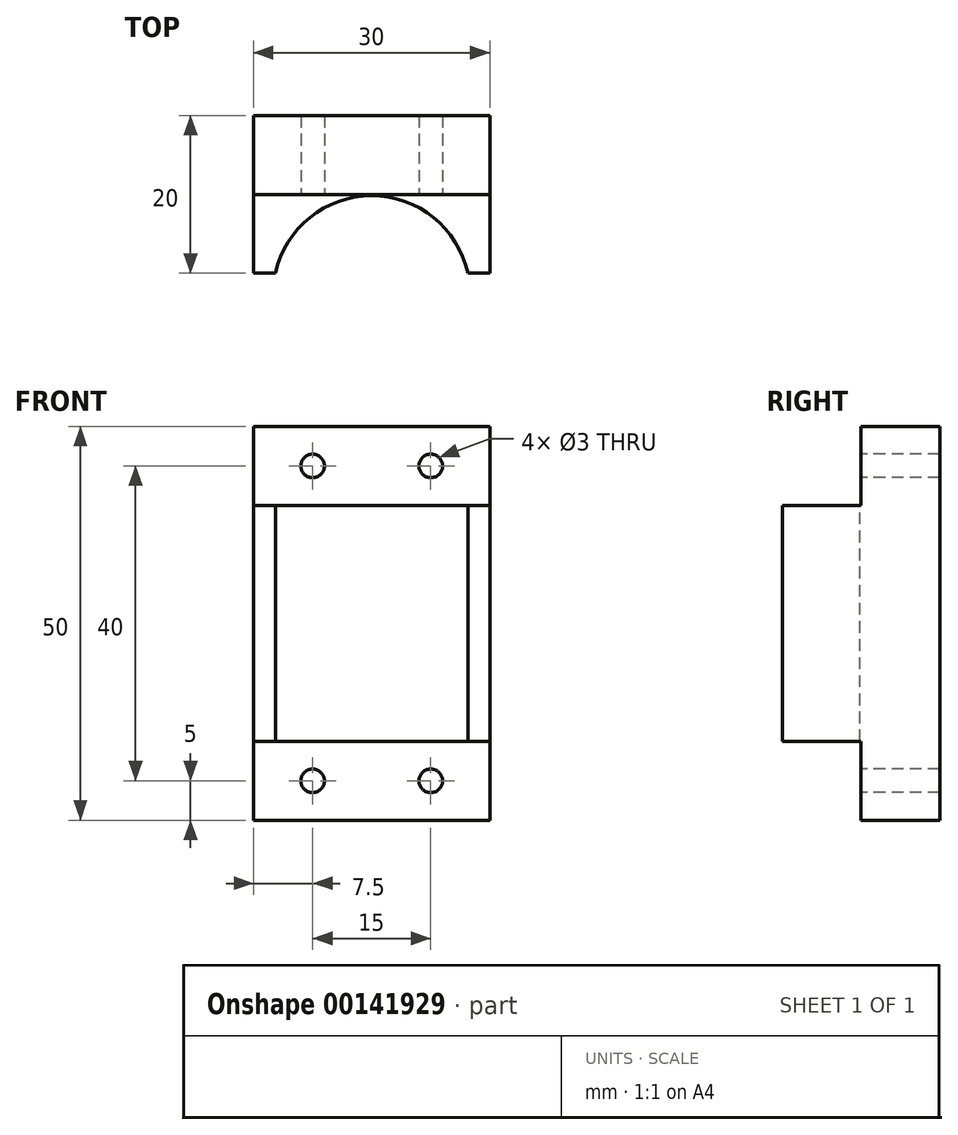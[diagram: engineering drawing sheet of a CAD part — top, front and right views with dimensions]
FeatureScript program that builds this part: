
annotation { "Feature Type Name" : "Feature", "Feature Type Description" : "" }
export const myFeature = defineFeature(function(context is Context, id is Id, definition is map)
    precondition{}
    {
        {
            var Q0;
            Q0=qCreatedBy(makeId("Front.planeOp"),FACE);
            var sketch = newSketch(context, id + "F0", { "sketchPlane" : qUnion([Q0])});
            skLineSegment(sketch, "E0.bottom", {"start": v(15, 25) * mm, "end": v(-15, 25) * mm});
            skLineSegment(sketch, "E0.top", {"start": v(15, -25) * mm, "end": v(-15, -25) * mm});
            skLineSegment(sketch, "E0.left", {"start": v(15, 25) * mm, "end": v(15, -25) * mm});
            skLineSegment(sketch, "E0.right", {"start": v(-15, 25) * mm, "end": v(-15, -25) * mm});
            skPoint(sketch, "E0.middle", {"position": v(0, 0) * mm});
            skSolve(sketch);
        }
        {
            var Q0;
            Q0 = qSketchRegion(id + "F0", true);
            extrude(context, id + "F1", {"entities" : qUnion([Q0]), "depth" : 10 * mm});
        }
        {
            var Q0;
            Q0=makeQuery(id+"F1.opExtrude","CAP_FACE",FACE,{"disambiguationData":[OSD([sQuery(id+"F0.wireOp",EDGE,"E0.bottom"),sQuery(id+"F0.wireOp",EDGE,"E0.top"),sQuery(id+"F0.wireOp",EDGE,"E0.left"),sQuery(id+"F0.wireOp",EDGE,"E0.right")])],"isStart":false});
            var sketch = newSketch(context, id + "F2", { "sketchPlane" : qUnion([Q0])});
            skCircle(sketch, "E1", {"center": v(7.5, -20) * mm, "radius": 1.5 * mm});
            skCircle(sketch, "E2", {"center": v(-7.5, -20) * mm, "radius": 1.5 * mm});
            skCircle(sketch, "E3", {"center": v(7.5, 20) * mm, "radius": 1.5 * mm});
            skCircle(sketch, "E4", {"center": v(-7.5, 20) * mm, "radius": 1.5 * mm});
            skSolve(sketch);
        }
        {
            var Q0;
            Q0 = qSketchRegion(id + "F2", true);
            extrude(context, id + "F3", {"entities" : qUnion([Q0]), "operationType" : NewBodyOperationType.REMOVE, "endBound" : BoundingType.THROUGH_ALL, "oppositeDirection" : true, "depth" : 25 * mm});
        }
        {
            var Q0;
            Q0=makeQuery(id+"F1.opExtrude","CAP_FACE",FACE,{"disambiguationData":[OSD([sQuery(id+"F0.wireOp",EDGE,"E0.bottom"),sQuery(id+"F0.wireOp",EDGE,"E0.top"),sQuery(id+"F0.wireOp",EDGE,"E0.left"),sQuery(id+"F0.wireOp",EDGE,"E0.right")])],"isStart":false});
            var sketch = newSketch(context, id + "F4", { "sketchPlane" : qUnion([Q0])});
            skLineSegment(sketch, "E5.bottom", {"start": v(15, 15) * mm, "end": v(-15, 15) * mm});
            skLineSegment(sketch, "E5.top", {"start": v(15, -15) * mm, "end": v(-15, -15) * mm});
            skLineSegment(sketch, "E5.left", {"start": v(15, 15) * mm, "end": v(15, -15) * mm});
            skLineSegment(sketch, "E5.right", {"start": v(-15, 15) * mm, "end": v(-15, -15) * mm});
            skPoint(sketch, "E5.middle", {"position": v(0, 0) * mm});
            skSolve(sketch);
        }
        {
            var Q0;
            Q0 = qSketchRegion(id + "F4", true);
            extrude(context, id + "F5", {"entities" : qUnion([Q0]), "operationType" : NewBodyOperationType.ADD, "depth" : 10 * mm});
        }
        {
            var Q0;
            Q0=qCreatedBy(makeId("Top.planeOp"),FACE);
            var sketch = newSketch(context, id + "F6", { "sketchPlane" : qUnion([Q0])});
            skCircle(sketch, "E6", {"center": v(0, -22.67) * mm, "radius": 12.5 * mm});
            skSolve(sketch);
        }
        {
            var Q0;
            Q0 = qSketchRegion(id + "F6", true);
            extrude(context, id + "F7", {"entities" : qUnion([Q0]), "operationType" : NewBodyOperationType.REMOVE, "endBound" : BoundingType.THROUGH_ALL, "oppositeDirection" : true, "depth" : 25 * mm});
        }
        {
            var Q0;
            Q0 = qSketchRegion(id + "F6", true);
            extrude(context, id + "F8", {"entities" : qUnion([Q0]), "operationType" : NewBodyOperationType.REMOVE, "endBound" : BoundingType.THROUGH_ALL, "depth" : 25 * mm});
        }
    });
